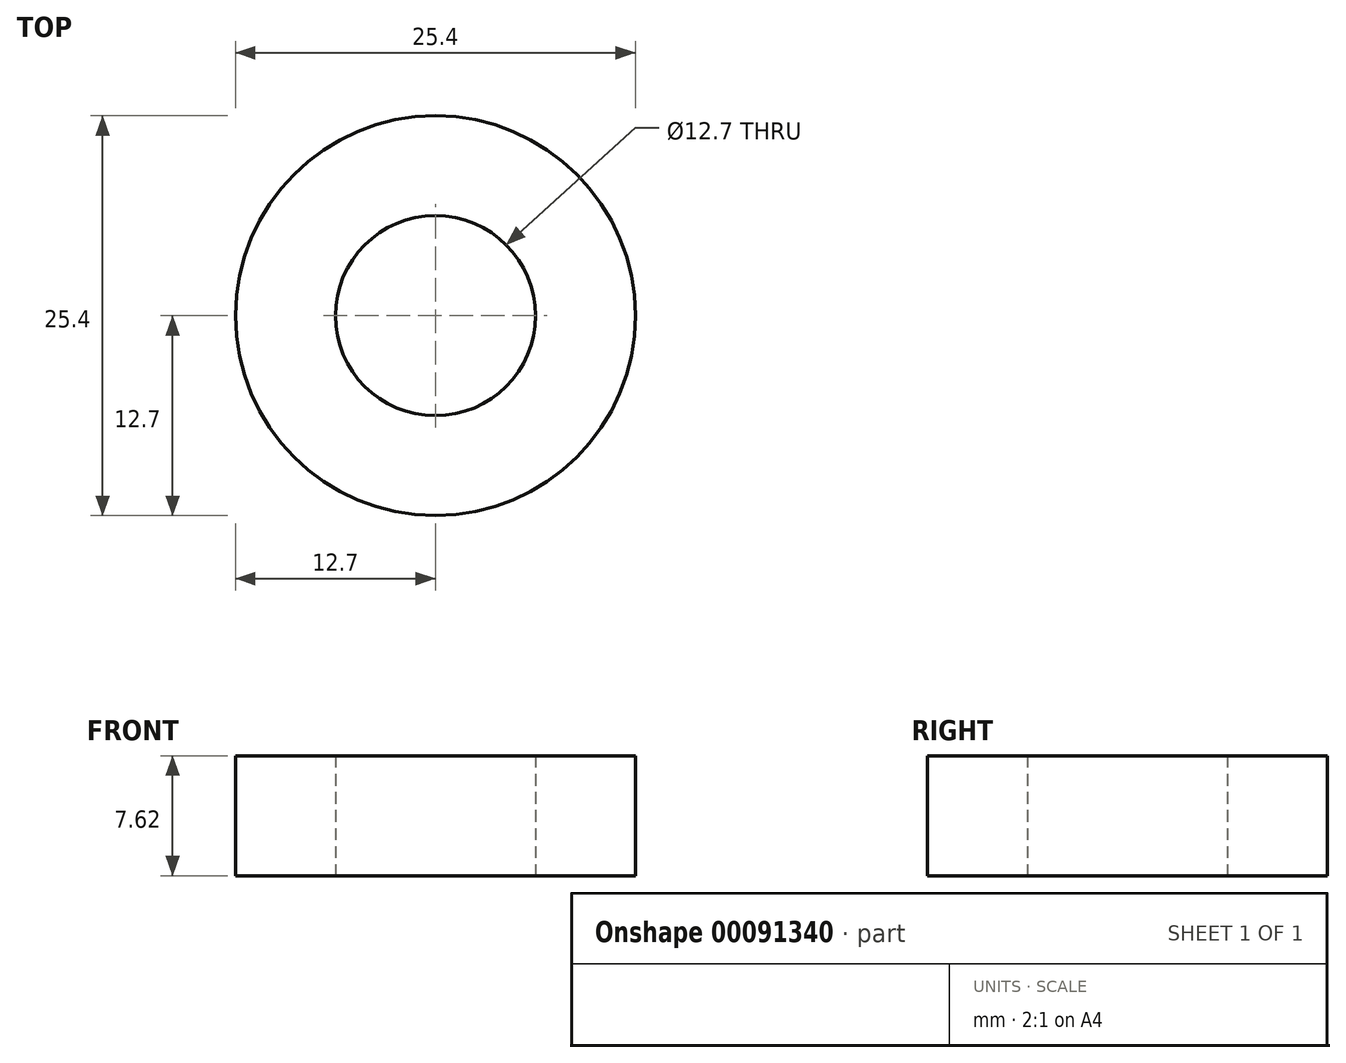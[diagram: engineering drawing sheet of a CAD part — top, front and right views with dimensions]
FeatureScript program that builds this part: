
annotation { "Feature Type Name" : "Feature", "Feature Type Description" : "" }
export const myFeature = defineFeature(function(context is Context, id is Id, definition is map)
    precondition{}
    {
        {
            var Q0;
            Q0=qCreatedBy(makeId("Top.planeOp"),FACE);
            var sketch = newSketch(context, id + "F0", { "sketchPlane" : qUnion([Q0])});
            skCircle(sketch, "E0", {"center": v(0, 0) * mm, "radius": 6.35 * mm});
            skCircle(sketch, "E1", {"center": v(0, 0) * mm, "radius": 12.7 * mm});
            skSolve(sketch);
        }
        {
            var Q0;
            Q0=makeQuery(id+"F0.imprint","IMPRINT",FACE,{"disambiguationData":[TD([[makeQuery(id+"F0.imprint","IMPRINT",EDGE,{"derivedFrom":sQuery(id+"F0.wireOp",EDGE,"E0")}),-1.0]])]});
            extrude(context, id + "F1", {"entities" : qUnion([Q0]), "depth" : 7.62 * mm});
        }
    });
